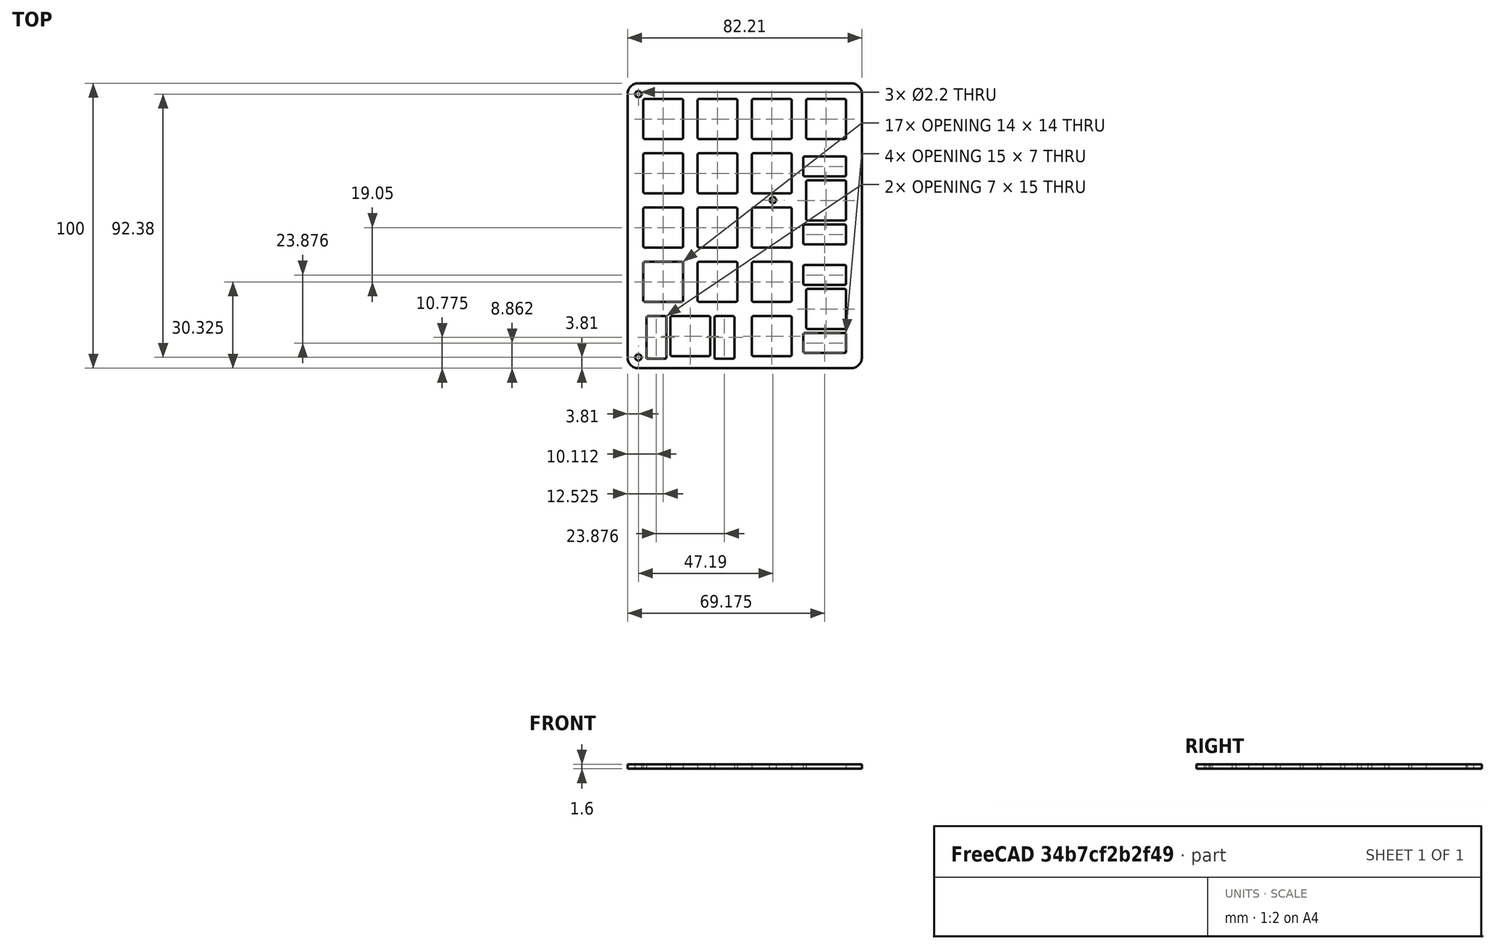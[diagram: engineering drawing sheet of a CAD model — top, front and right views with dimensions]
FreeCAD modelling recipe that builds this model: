
FCSTD DOCUMENT  (FreeCAD 0.19R24267 (Git))
Label: quartet_plate_numpad
License: All rights reserved
LicenseURL: http://en.wikipedia.org/wiki/All_rights_reserved
objects: App::Part×3, PartDesign::CoordinateSystem×1, Part::Feature×1, Sketcher::SketchObject×1
note: 3 computed .brp shape members not serialized (recipe doc carries the construction recipe); baked Part::Feature solids carry a one-line shape summary decoded from their .brp

FEATURE [PartDesign::CoordinateSystem] Local_CS_3e6e
  AttacherType = Attacher::AttachEngine3D
FEATURE [Part::Feature] Pcb_3e6e
  shape: bbox 82.21 x 100 x 1.6 mm, 197 faces (baked)
FEATURE [Sketcher::SketchObject] PCB_Sketch_3e6e
  FullyConstrained = false
  sketch-geometry (8):
    g0: LineSegment StartX=3.81 StartY=-4e-16 StartZ=0 EndX=78.4 EndY=-4.9e-15 EndZ=0
    g1: LineSegment StartX=82.21 StartY=-3.81 StartZ=0 EndX=82.21 EndY=-96.19 EndZ=0
    g2: LineSegment StartX=78.4 StartY=-100 StartZ=0 EndX=3.81 EndY=-100 EndZ=0
    g3: LineSegment StartX=-7.5e-15 StartY=-96.19 StartZ=0 EndX=4e-16 EndY=-3.81 EndZ=0
    g4: ArcOfCircle CenterX=3.81 CenterY=-3.81 CenterZ=0 NormalX=0 NormalY=0 NormalZ=1 AngleXU=0 Radius=3.81 StartAngle=1.5708 EndAngle=3.14159
    g5: ArcOfCircle CenterX=3.81 CenterY=-96.19 CenterZ=0 NormalX=0 NormalY=0 NormalZ=1 AngleXU=0 Radius=3.81 StartAngle=3.14159 EndAngle=4.71239
    g6: ArcOfCircle CenterX=78.4 CenterY=-96.19 CenterZ=0 NormalX=0 NormalY=0 NormalZ=1 AngleXU=0 Radius=3.81 StartAngle=4.71239 EndAngle=6.28319
    g7: ArcOfCircle CenterX=78.4 CenterY=-3.81 CenterZ=0 NormalX=0 NormalY=0 NormalZ=1 AngleXU=0 Radius=3.81 StartAngle=0 EndAngle=1.5708
  constraints (8):
    c: Coincident(g3,g5)
    c: Coincident(g3,g4)
    c: Coincident(g2,g5)
    c: Coincident(g0,g4)
    c: Coincident(g2,g6)
    c: Coincident(g0,g7)
    c: Coincident(g1,g6)
    c: Coincident(g1,g7)
FEATURE [App::Part] Board_Geoms_3e6e
  Group = -> [Local_CS_3e6e,Pcb_3e6e,PCB_Sketch_3e6e]
  Origin = -> Origin
FEATURE [App::Part] Step_Models_3e6e
  Origin = -> Origin002
FEATURE [App::Part] Board_3e6e  label="quartet_plate_numpad"
  Group = -> [Board_Geoms_3e6e,Step_Models_3e6e]
  Origin = -> Origin001
